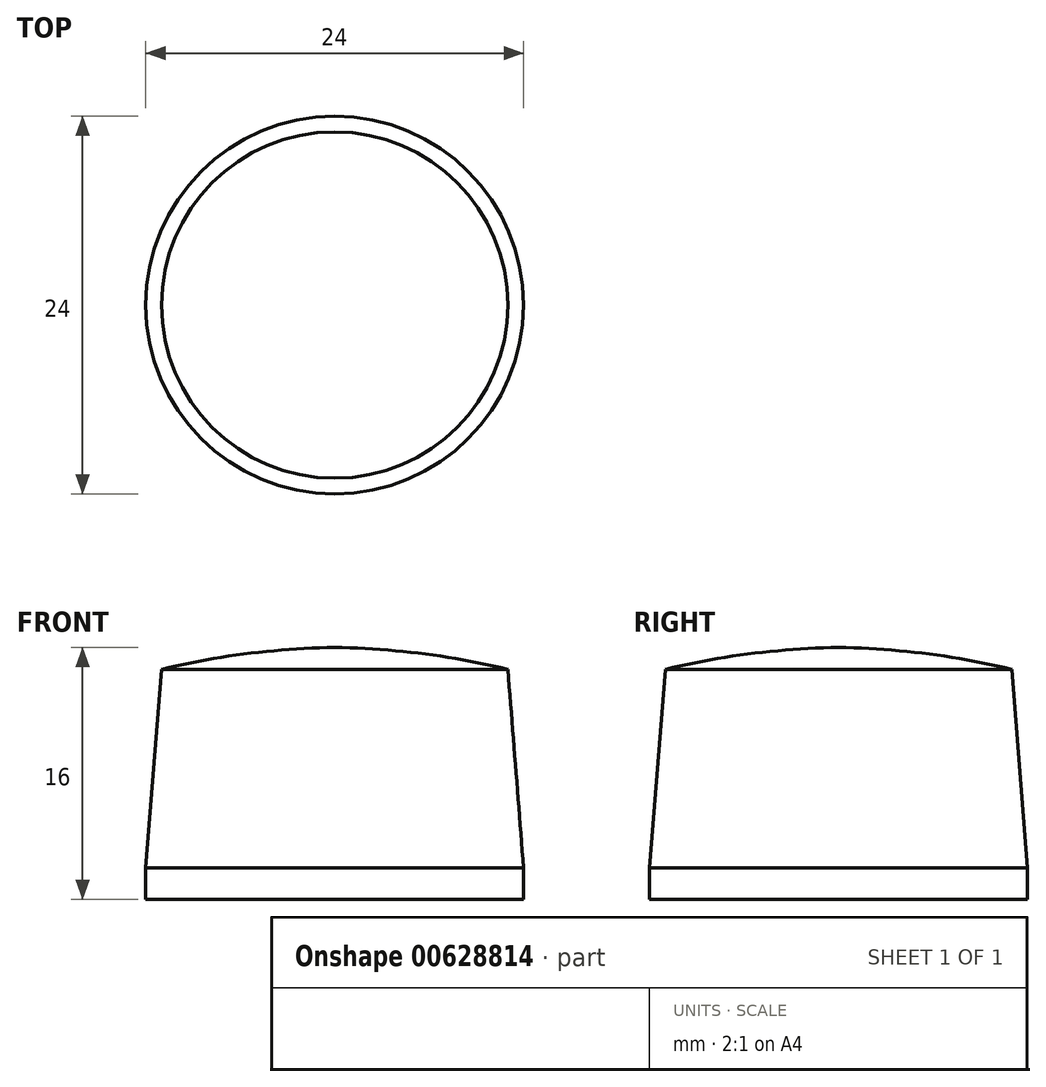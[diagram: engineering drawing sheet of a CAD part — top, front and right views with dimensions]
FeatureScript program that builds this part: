
annotation { "Feature Type Name" : "Feature", "Feature Type Description" : "" }
export const myFeature = defineFeature(function(context is Context, id is Id, definition is map)
    precondition{}
    {
        {
            var Q0;
            Q0=qCreatedBy(makeId("Front.planeOp"),FACE);
            var sketch = newSketch(context, id + "F0", { "sketchPlane" : qUnion([Q0])});
            skLineSegment(sketch, "E0", {"start": v(-12, -0.74) * mm, "end": v(-11, 11.88) * mm});
            skLineSegment(sketch, "E1", {"start": v(-12, -0.74) * mm, "end": v(-12, -2.74) * mm});
            skLineSegment(sketch, "E2", {"start": v(-12, -2.74) * mm, "end": v(0, -2.74) * mm});
            skPoint(sketch, "E3.start.orphan", {"position": v(0, -9.65) * mm});
            skArc(sketch, "E4", {"start": v(0, 13.26) * mm, "mid": v(-5.54, 12.87) * mm, "end": v(-11, 11.88) * mm});
            skLineSegment(sketch, "E5", {"start": v(0, 13.26) * mm, "end": v(0, -2.74) * mm});
            skLineSegment(sketch, "E6", {"start": v(0, 35.45) * mm, "end": v(0, -22.13) * mm, "construction": true});
            skSolve(sketch);
        }
        {
            var Q0;
            Q0 = qSketchRegion(id + "F0", true);
            var Q1;
            Q1=sQuery(id+"F0.wireOp",EDGE,"E6");
            revolve(context, id + "F1", {"entities" : qUnion([Q0]), "axis" : qUnion([Q1]), "revolveType" : RevolveType.FULL});
        }
    });
